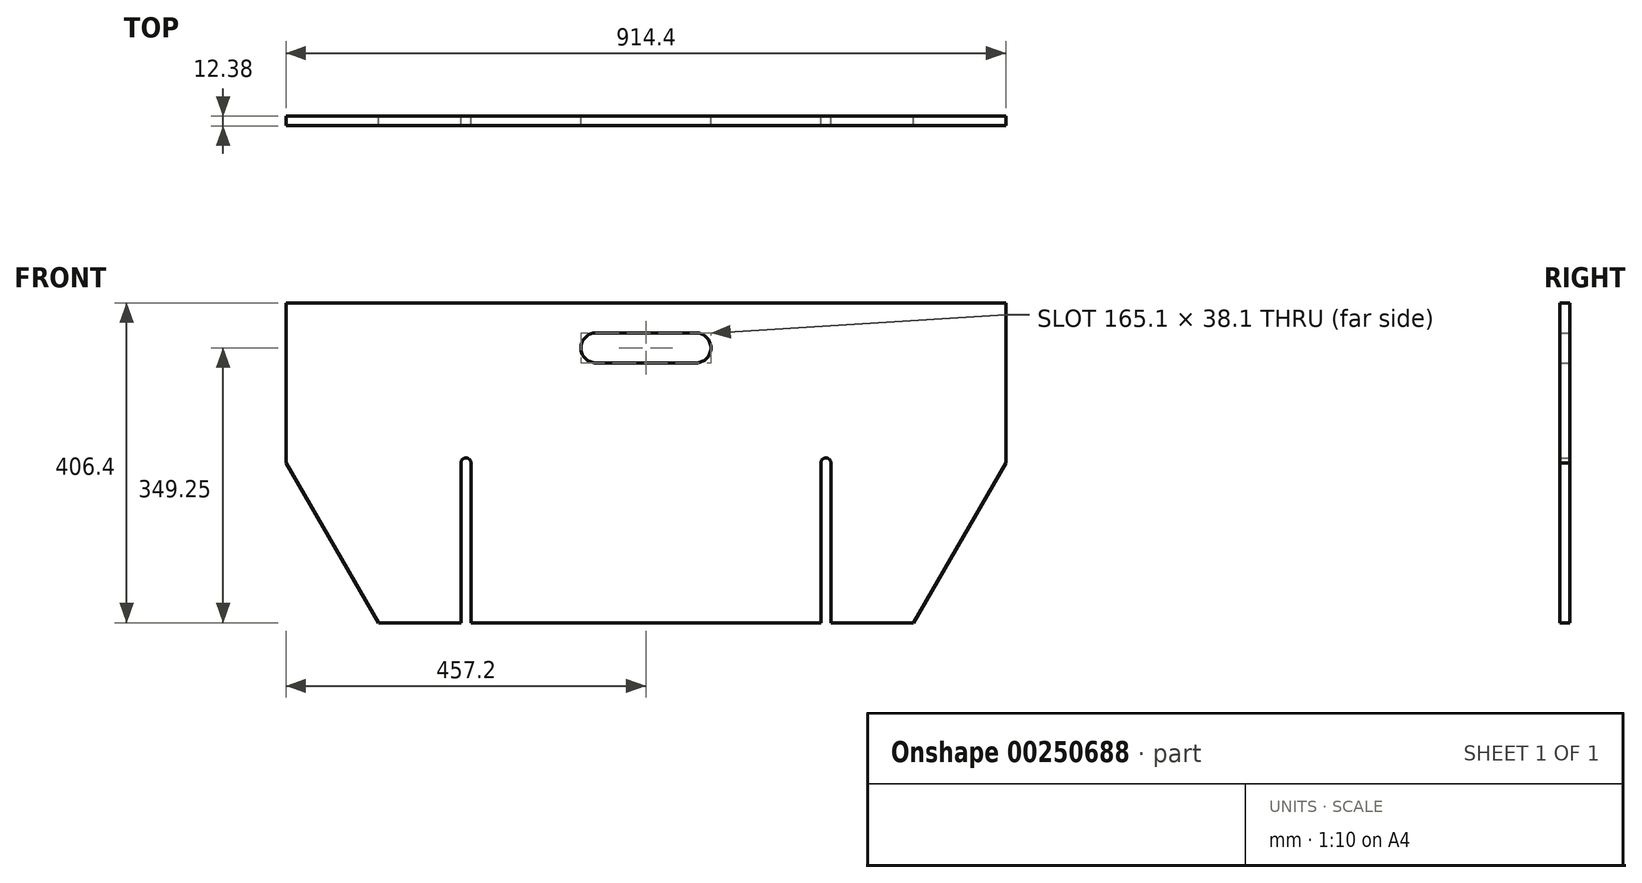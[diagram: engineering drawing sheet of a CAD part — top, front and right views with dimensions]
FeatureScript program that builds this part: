
annotation { "Feature Type Name" : "Feature", "Feature Type Description" : "" }
export const myFeature = defineFeature(function(context is Context, id is Id, definition is map)
    precondition{}
    {
        {
            assignVariable(context, id + "F0", {"name" : "Thickness", "anyValue" : 15 / 32});
        }
        {
            var Q0;
            Q0=qCreatedBy(makeId("Front.planeOp"),FACE);
            var sketch = newSketch(context, id + "F1", { "sketchPlane" : qUnion([Q0])});
            skLineSegment(sketch, "E0.bottom", {"start": v(0, 406.4) * mm, "end": v(914.4, 406.4) * mm});
            skLineSegment(sketch, "E0.top", {"start": v(117.32, 0) * mm, "end": v(222.25, 0) * mm});
            skLineSegment(sketch, "E0.left", {"start": v(0, 406.4) * mm, "end": v(0, 203.2) * mm});
            skLineSegment(sketch, "E0.right", {"start": v(914.4, 406.4) * mm, "end": v(914.4, 0) * mm, "construction": true});
            skLineSegment(sketch, "E1", {"start": v(0, 203.2) * mm, "end": v(117.32, 0) * mm});
            skPoint(sketch, "E2", {"position": v(228.6, 0) * mm});
            skPoint(sketch, "E3", {"position": v(685.8, 0) * mm});
            skLineSegment(sketch, "E4", {"start": v(685.8, 0) * mm, "end": v(685.8, 203.2) * mm, "construction": true});
            skLineSegment(sketch, "E5", {"start": v(228.6, 0) * mm, "end": v(228.6, 203.2) * mm, "construction": true});
            skArc(sketch, "E6", {"start": v(234.95, 203.2) * mm, "mid": v(228.6, 209.55) * mm, "end": v(222.25, 203.2) * mm});
            skPoint(sketch, "E7.orphan", {"position": v(0, 0) * mm});
            skArc(sketch, "E8", {"start": v(692.15, 203.2) * mm, "mid": v(685.8, 209.55) * mm, "end": v(679.45, 203.2) * mm});
            skLineSegment(sketch, "E9", {"start": v(222.25, 203.2) * mm, "end": v(222.25, 0) * mm});
            skLineSegment(sketch, "E10", {"start": v(234.95, 203.2) * mm, "end": v(234.95, 0) * mm});
            skLineSegment(sketch, "E11", {"start": v(679.45, 203.2) * mm, "end": v(679.45, 0) * mm});
            skLineSegment(sketch, "E12", {"start": v(692.15, 203.2) * mm, "end": v(692.15, 0) * mm});
            skLineSegment(sketch, "E13.trimOffspring", {"start": v(692.15, 0) * mm, "end": v(797.08, 0) * mm});
            skLineSegment(sketch, "E14.trimOffspring", {"start": v(234.95, 0) * mm, "end": v(679.45, 0) * mm});
            skLineSegment(sketch, "E15", {"start": v(457.2, 406.4) * mm, "end": v(457.2, 368.3) * mm, "construction": true});
            skLineSegment(sketch, "E16", {"start": v(457.2, 368.3) * mm, "end": v(393.7, 368.3) * mm});
            skLineSegment(sketch, "E17", {"start": v(457.2, 368.3) * mm, "end": v(457.2, 330.2) * mm, "construction": true});
            skLineSegment(sketch, "E18", {"start": v(457.2, 330.2) * mm, "end": v(393.7, 330.2) * mm});
            skArc(sketch, "E19", {"start": v(393.7, 368.3) * mm, "mid": v(374.65, 349.25) * mm, "end": v(393.7, 330.2) * mm});
            skLineSegment(sketch, "E20.MirrorCS", {"start": v(457.2, 368.3) * mm, "end": v(520.7, 368.3) * mm});
            skArc(sketch, "E21.MirrorCS", {"start": v(520.7, 368.3) * mm, "mid": v(539.75, 349.25) * mm, "end": v(520.7, 330.2) * mm});
            skLineSegment(sketch, "E22.MirrorCS", {"start": v(457.2, 330.2) * mm, "end": v(520.7, 330.2) * mm});
            skLineSegment(sketch, "E23", {"start": v(914.4, 203.2) * mm, "end": v(797.08, 0) * mm});
            skPoint(sketch, "E24.orphan", {"position": v(914.4, 0) * mm});
            skLineSegment(sketch, "E25", {"start": v(914.4, 406.4) * mm, "end": v(914.4, 203.2) * mm});
            skSolve(sketch);
        }
        {
            var Q0;
            Q0=makeQuery(id+"F1.imprint","IMPRINT",FACE,{"disambiguationData":[TD([[makeQuery(id+"F1.imprint","IMPRINT",EDGE,{"derivedFrom":sQuery(id+"F1.wireOp",EDGE,"E0.bottom")}),-1.0]])]});
            extrude(context, id + "F2", {"entities" : qUnion([Q0]), "depth" : (getVariable(context, 'Thickness')) * mm});
        }
        {
            var Q0;
            Q0=makeQuery(id+"F2.opExtrude","CAP_FACE",FACE,{"disambiguationData":[OSD([sQuery(id+"F1.wireOp",EDGE,"E0.bottom"),sQuery(id+"F1.wireOp",EDGE,"E0.top"),sQuery(id+"F1.wireOp",EDGE,"E0.left"),sQuery(id+"F1.wireOp",EDGE,"E1"),sQuery(id+"F1.wireOp",EDGE,"E6"),sQuery(id+"F1.wireOp",EDGE,"E8"),sQuery(id+"F1.wireOp",EDGE,"E9"),sQuery(id+"F1.wireOp",EDGE,"E10"),sQuery(id+"F1.wireOp",EDGE,"E11"),sQuery(id+"F1.wireOp",EDGE,"E12"),sQuery(id+"F1.wireOp",EDGE,"E13.trimOffspring"),sQuery(id+"F1.wireOp",EDGE,"E14.trimOffspring"),sQuery(id+"F1.wireOp",EDGE,"E16"),sQuery(id+"F1.wireOp",EDGE,"E18"),sQuery(id+"F1.wireOp",EDGE,"E19"),sQuery(id+"F1.wireOp",EDGE,"E20.MirrorCS"),sQuery(id+"F1.wireOp",EDGE,"E21.MirrorCS"),sQuery(id+"F1.wireOp",EDGE,"E22.MirrorCS"),sQuery(id+"F1.wireOp",EDGE,"E23"),sQuery(id+"F1.wireOp",EDGE,"E25")])],"isStart":false});
            extrude(context, id + "F3", {"entities" : qUnion([Q0]), "operationType" : NewBodyOperationType.ADD, "depth" : 11.9 * mm});
        }
    });
